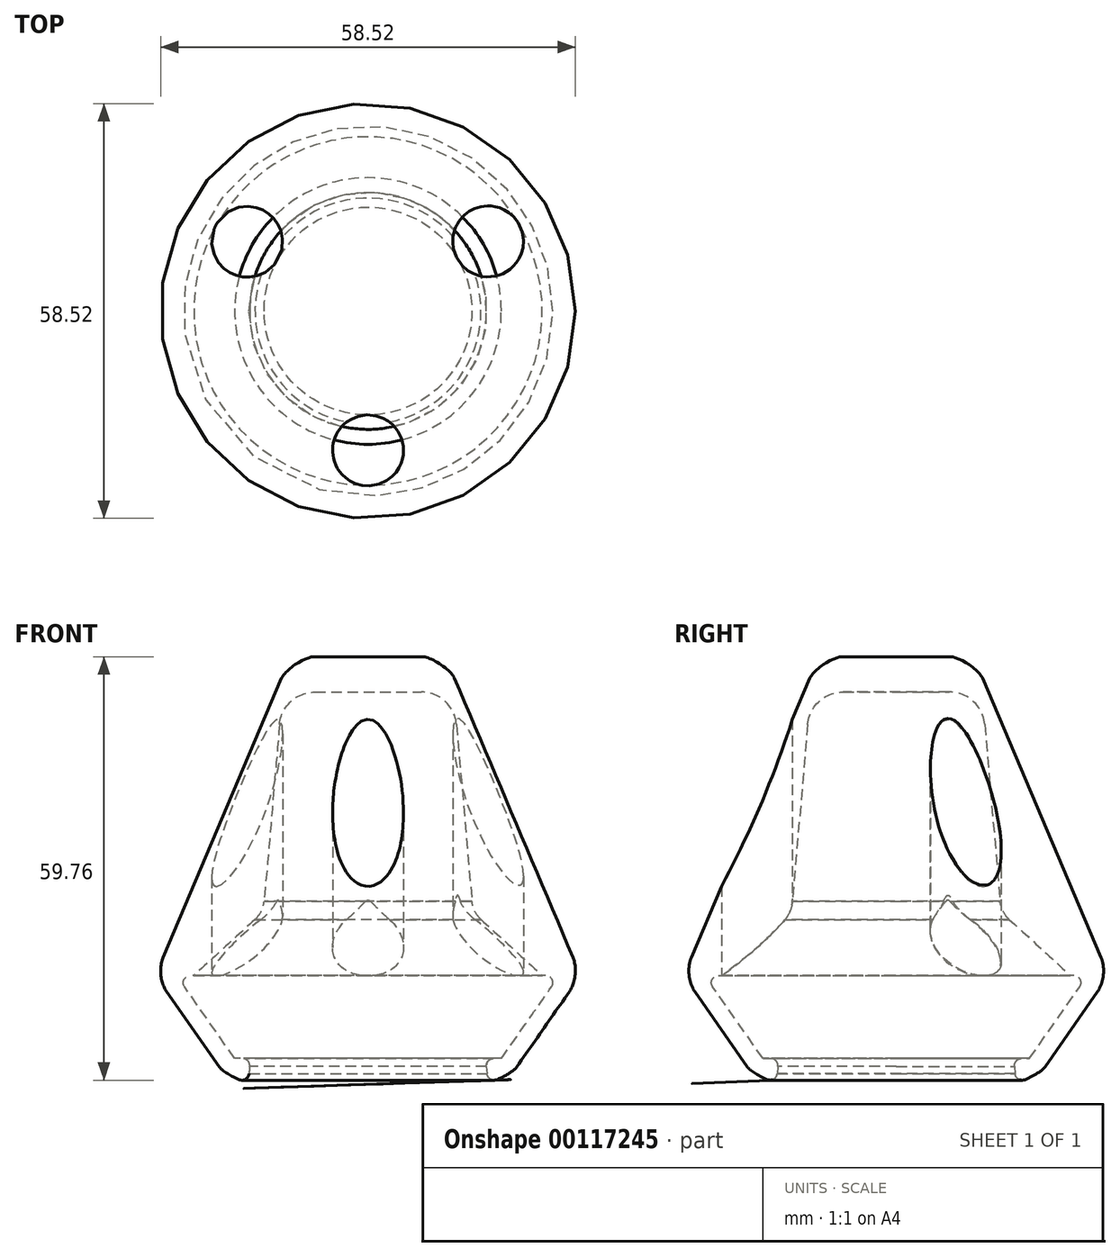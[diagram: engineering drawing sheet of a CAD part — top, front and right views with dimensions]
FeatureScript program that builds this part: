
annotation { "Feature Type Name" : "Feature", "Feature Type Description" : "" }
export const myFeature = defineFeature(function(context is Context, id is Id, definition is map)
    precondition{}
    {
        {
            var Q0;
            Q0=qCreatedBy(makeId("Top.planeOp"),FACE);
            var sketch = newSketch(context, id + "F0", { "sketchPlane" : qUnion([Q0])});
            skCircle(sketch, "E0", {"center": v(0, 0) * mm, "radius": 30 * mm});
            skCircle(sketch, "E1", {"center": v(0, -19.65) * mm, "radius": 5 * mm});
            skCircle(sketch, "E2", {"center": v(-17.05, 9.76) * mm, "radius": 5 * mm});
            skCircle(sketch, "E3", {"center": v(16.95, 9.82) * mm, "radius": 5 * mm});
            skSolve(sketch);
        }
        {
            var Q0;
            Q0=makeQuery(id+"F0.imprint","IMPRINT",FACE,{"disambiguationData":[TD([[makeQuery(id+"F0.imprint","IMPRINT",EDGE,{"derivedFrom":sQuery(id+"F0.wireOp",EDGE,"E0")}),1.0]])]});
            var Q1;
            Q1=makeQuery(id+"F0.imprint","IMPRINT",FACE,{"disambiguationData":[TD([[makeQuery(id+"F0.imprint","IMPRINT",EDGE,{"derivedFrom":sQuery(id+"F0.wireOp",EDGE,"E1")}),1.0]])]});
            var Q2;
            Q2=makeQuery(id+"F0.imprint","IMPRINT",FACE,{"disambiguationData":[TD([[makeQuery(id+"F0.imprint","IMPRINT",EDGE,{"derivedFrom":sQuery(id+"F0.wireOp",EDGE,"E3")}),1.0]])]});
            var Q3;
            Q3=makeQuery(id+"F0.imprint","IMPRINT",FACE,{"disambiguationData":[TD([[makeQuery(id+"F0.imprint","IMPRINT",EDGE,{"derivedFrom":sQuery(id+"F0.wireOp",EDGE,"E2")}),1.0]])]});
            extrude(context, id + "F1", {"entities" : qUnion([Q0, Q1, Q2, Q3]), "oppositeDirection" : true, "depth" : 15 * mm, "offsetDistance" : 25 * mm, "hasDraft" : true, "draftAngle" : 35 * degree, "draftPullDirection" : true});
        }
        {
            var Q0;
            Q0=makeQuery(id+"F0.imprint","IMPRINT",FACE,{"disambiguationData":[TD([[makeQuery(id+"F0.imprint","IMPRINT",EDGE,{"derivedFrom":sQuery(id+"F0.wireOp",EDGE,"E0")}),1.0]])]});
            var Q1;
            Q1=makeQuery(id+"F1.opExtrude","CAP_FACE",FACE,{"disambiguationData":[OSD([sQuery(id+"F0.wireOp",EDGE,"E0")])],"isStart":false});
            var Q2;
            Q2=makeQuery(id+"F0.imprint","IMPRINT",FACE,{"disambiguationData":[TD([[makeQuery(id+"F0.imprint","IMPRINT",EDGE,{"derivedFrom":sQuery(id+"F0.wireOp",EDGE,"E3")}),1.0]])]});
            var Q3;
            Q3=makeQuery(id+"F0.imprint","IMPRINT",FACE,{"disambiguationData":[TD([[makeQuery(id+"F0.imprint","IMPRINT",EDGE,{"derivedFrom":sQuery(id+"F0.wireOp",EDGE,"E1")}),1.0]])]});
            var Q4;
            Q4=makeQuery(id+"F0.imprint","IMPRINT",FACE,{"disambiguationData":[TD([[makeQuery(id+"F0.imprint","IMPRINT",EDGE,{"derivedFrom":sQuery(id+"F0.wireOp",EDGE,"E2")}),1.0]])]});
            extrude(context, id + "F2", {"entities" : qUnion([Q0, Q1, Q2, Q3, Q4]), "operationType" : NewBodyOperationType.ADD, "depth" : 45 * mm, "offsetDistance" : 25 * mm, "hasDraft" : true, "draftAngle" : 23 * degree, "draftPullDirection" : true});
        }
        {
            var Q0;
            {var subQ0=sQuery(id+"F0.wireOp",EDGE,"E0");Q0=makeQuery(id+"F2.boolean.opBoolean","MERGE",EDGE,{"derivedFrom":[makeQuery(id+"F1.opExtrude","CAP_EDGE",EDGE,{"disambiguationData":[OSD([subQ0])],"isStart":true}),makeQuery(id+"F2.opExtrude","CAP_EDGE",EDGE,{"disambiguationData":[OSD([subQ0]),TDD([makeQuery(id+"F0.imprint","IMPRINT",EDGE,{"derivedFrom":subQ0})])],"isStart":true})]});}
            fillet(context, id + "F3", {"entities" : qUnion([Q0]), "radius" : 5 * mm, "tangentPropagation" : true, "rho" : .42, "crossSection" : FilletCrossSection.CONIC, "allowEdgeOverflow" : false});
        }
        {
            var Q0;
            Q0=makeQuery(id+"F1.opExtrude","CAP_EDGE",EDGE,{"disambiguationData":[OSD([sQuery(id+"F0.wireOp",EDGE,"E0")])],"isStart":false});
            var Q1;
            {var subQ0=sQuery(id+"F0.wireOp",EDGE,"E0");Q1=makeQuery(id+"F2.opExtrude","CAP_EDGE",EDGE,{"disambiguationData":[OSD([subQ0]),TDD([makeQuery(id+"F0.imprint","IMPRINT",EDGE,{"derivedFrom":subQ0})])],"isStart":false});}
            fillet(context, id + "F4", {"entities" : qUnion([Q0, Q1]), "radius" : 5 * mm, "tangentPropagation" : true, "rho" : .3, "crossSection" : FilletCrossSection.CONIC, "allowEdgeOverflow" : false});
        }
        {
            var Q0;
            Q0=makeQuery(id+"F0.imprint","IMPRINT",FACE,{"disambiguationData":[TD([[makeQuery(id+"F0.imprint","IMPRINT",EDGE,{"derivedFrom":sQuery(id+"F0.wireOp",EDGE,"E1")}),1.0]])]});
            var Q1;
            Q1=makeQuery(id+"F0.imprint","IMPRINT",FACE,{"disambiguationData":[TD([[makeQuery(id+"F0.imprint","IMPRINT",EDGE,{"derivedFrom":sQuery(id+"F0.wireOp",EDGE,"E2")}),1.0]])]});
            var Q2;
            Q2=makeQuery(id+"F0.imprint","IMPRINT",FACE,{"disambiguationData":[TD([[makeQuery(id+"F0.imprint","IMPRINT",EDGE,{"derivedFrom":sQuery(id+"F0.wireOp",EDGE,"E3")}),1.0]])]});
            extrude(context, id + "F5", {"entities" : qUnion([Q0, Q1, Q2]), "operationType" : NewBodyOperationType.REMOVE, "endBound" : BoundingType.UP_TO_NEXT, "depth" : 25 * mm, "offsetDistance" : 25 * mm});
        }
        {
            var Q0;
            Q0=makeQuery(id+"F1.opExtrude","CAP_FACE",FACE,{"disambiguationData":[OSD([sQuery(id+"F0.wireOp",EDGE,"E0")])],"isStart":false});
            extrude(context, id + "F6", {"entities" : qUnion([Q0]), "operationType" : NewBodyOperationType.REMOVE, "oppositeDirection" : true, "depth" : 55 * mm, "offsetDistance" : 25 * mm, "hasDraft" : true, "draftAngle" : 5 * degree, "draftPullDirection" : true});
        }
        {
            var Q0;
            Q0=makeQuery(id+"F6.boolean.opBoolean","INTERSECT",EDGE,{"derivedFrom":[makeQuery(id+"F5.boolean.opBoolean","COPY",FACE,{"derivedFrom":makeQuery(id+"F5.opExtrude","CAP_FACE",FACE,{"disambiguationData":[OSD([sQuery(id+"F0.wireOp",EDGE,"E2")])],"isStart":true})}),makeQuery(id+"F6.opExtrude","SWEPT_FACE",FACE,{"disambiguationData":[OSD([sQuery(id+"F0.wireOp",EDGE,"E0")])]})]});
            var Q1;
            Q1=makeQuery(id+"F6.boolean.opBoolean","INTERSECT",EDGE,{"derivedFrom":[makeQuery(id+"F5.boolean.opBoolean","COPY",FACE,{"derivedFrom":makeQuery(id+"F5.opExtrude","CAP_FACE",FACE,{"disambiguationData":[OSD([sQuery(id+"F0.wireOp",EDGE,"E1")])],"isStart":true})}),makeQuery(id+"F6.opExtrude","SWEPT_FACE",FACE,{"disambiguationData":[OSD([sQuery(id+"F0.wireOp",EDGE,"E0")])]})]});
            var Q2;
            Q2=makeQuery(id+"F6.boolean.opBoolean","INTERSECT",EDGE,{"derivedFrom":[makeQuery(id+"F5.boolean.opBoolean","COPY",FACE,{"derivedFrom":makeQuery(id+"F5.opExtrude","CAP_FACE",FACE,{"disambiguationData":[OSD([sQuery(id+"F0.wireOp",EDGE,"E3")])],"isStart":true})}),makeQuery(id+"F6.opExtrude","SWEPT_FACE",FACE,{"disambiguationData":[OSD([sQuery(id+"F0.wireOp",EDGE,"E0")])]})]});
            chamfer(context, id + "F7", {"entities" : qUnion([Q0, Q1, Q2]), "width" : 7 * mm, "tangentPropagation" : true});
        }
        {
            var Q0;
            Q0=makeQuery(id+"F0.imprint","IMPRINT",FACE,{"disambiguationData":[TD([[makeQuery(id+"F0.imprint","IMPRINT",EDGE,{"derivedFrom":sQuery(id+"F0.wireOp",EDGE,"E0")}),1.0]])]});
            var Q1;
            Q1=makeQuery(id+"F0.imprint","IMPRINT",FACE,{"disambiguationData":[TD([[makeQuery(id+"F0.imprint","IMPRINT",EDGE,{"derivedFrom":sQuery(id+"F0.wireOp",EDGE,"E3")}),1.0]])]});
            var Q2;
            Q2=makeQuery(id+"F0.imprint","IMPRINT",FACE,{"disambiguationData":[TD([[makeQuery(id+"F0.imprint","IMPRINT",EDGE,{"derivedFrom":sQuery(id+"F0.wireOp",EDGE,"E1")}),1.0]])]});
            var Q3;
            Q3=makeQuery(id+"F0.imprint","IMPRINT",FACE,{"disambiguationData":[TD([[makeQuery(id+"F0.imprint","IMPRINT",EDGE,{"derivedFrom":sQuery(id+"F0.wireOp",EDGE,"E2")}),1.0]])]});
            extrude(context, id + "F8", {"entities" : qUnion([Q0, Q1, Q2, Q3]), "oppositeDirection" : true, "depth" : 13 * mm, "offsetDistance" : 25 * mm, "hasDraft" : true, "draftAngle" : 35 * degree, "draftPullDirection" : true});
        }
        {
            var Q0;
            Q0=makeQuery(id+"F8.opExtrude","SWEPT_BODY",BODY,{"disambiguationData":[OSD([sQuery(id+"F0.wireOp",EDGE,"E0")])]});
            var Q1;
            Q1=qCreatedBy(makeId("Origin.pointOp"),VERTEX);
            transform(context, id + "F9", {"entities" : qUnion([Q0]), "transformType" : TransformType.SCALE_UNIFORMLY, "scale" : .90, "scalePoint" : qUnion([Q1]), "makeCopy" : false});
        }
        {
            var Q0;
            Q0=makeQuery(id+"F8.opExtrude","SWEPT_BODY",BODY,{"disambiguationData":[OSD([sQuery(id+"F0.wireOp",EDGE,"E0")])]});
            var Q1;
            Q1=makeQuery(id+"F1.opExtrude","SWEPT_BODY",BODY,{"disambiguationData":[OSD([sQuery(id+"F0.wireOp",EDGE,"E0")])]});
            booleanBodies(context, id + "F10", {"operationType" : BooleanOperationType.SUBTRACTION, "tools" : qUnion([Q0]), "targets" : qUnion([Q1])});
        }
        {
            var Q0;
            {var subQ0=sQuery(id+"F0.wireOp",EDGE,"E0");Q0=makeQuery(id+"F10.opBoolean","INTERSECT",EDGE,{"disambiguationData":[OD(0.0)],"derivedFrom":[makeQuery(id+"F6.boolean.opBoolean","COPY",FACE,{"derivedFrom":makeQuery(id+"F6.opExtrude","SWEPT_FACE",FACE,{"disambiguationData":[OSD([subQ0])]})}),makeQuery(id+"F8.opExtrude","CAP_FACE",FACE,{"disambiguationData":[OSD([subQ0])],"isStart":true})]});}
            var Q1;
            {var subQ0=sQuery(id+"F0.wireOp",EDGE,"E0");Q1=makeQuery(id+"F10.opBoolean","INTERSECT",EDGE,{"disambiguationData":[OD(1.0)],"derivedFrom":[makeQuery(id+"F6.boolean.opBoolean","COPY",FACE,{"derivedFrom":makeQuery(id+"F6.opExtrude","SWEPT_FACE",FACE,{"disambiguationData":[OSD([subQ0])]})}),makeQuery(id+"F8.opExtrude","CAP_FACE",FACE,{"disambiguationData":[OSD([subQ0])],"isStart":true})]});}
            var Q2;
            {var subQ0=sQuery(id+"F0.wireOp",EDGE,"E0");Q2=makeQuery(id+"F10.opBoolean","INTERSECT",EDGE,{"disambiguationData":[OD(2.0)],"derivedFrom":[makeQuery(id+"F6.boolean.opBoolean","COPY",FACE,{"derivedFrom":makeQuery(id+"F6.opExtrude","SWEPT_FACE",FACE,{"disambiguationData":[OSD([subQ0])]})}),makeQuery(id+"F8.opExtrude","CAP_FACE",FACE,{"disambiguationData":[OSD([subQ0])],"isStart":true})]});}
            chamfer(context, id + "F11", {"entities" : qUnion([Q0, Q1, Q2]), "chamferType" : ChamferType.TWO_OFFSETS, "width1" : 9 * mm, "oppositeDirection" : false, "width2" : 9 * mm, "tangentPropagation" : true});
        }
        {
            var Q0;
            Q0=makeQuery(id+"F6.boolean.opBoolean","COPY",EDGE,{"derivedFrom":makeQuery(id+"F6.opExtrude","CAP_EDGE",EDGE,{"disambiguationData":[OSD([sQuery(id+"F0.wireOp",EDGE,"E0")])],"isStart":false})});
            fillet(context, id + "F12", {"entities" : qUnion([Q0]), "radius" : 5 * mm, "tangentPropagation" : true, "allowEdgeOverflow" : false});
        }
        {
            var Q0;
            {var subQ0=sQuery(id+"F0.wireOp",EDGE,"E0");var subQ1=makeQuery(id+"F8.opExtrude","CAP_FACE",FACE,{"disambiguationData":[OSD([subQ0])],"isStart":true});var subQ2=makeQuery(id+"F6.boolean.opBoolean","COPY",FACE,{"derivedFrom":makeQuery(id+"F6.opExtrude","SWEPT_FACE",FACE,{"disambiguationData":[OSD([subQ0])]})});Q0=makeQuery(id+"F11.opChamfer","BLEND_EDGE",EDGE,{"blendedFrom":[makeQuery(id+"F10.opBoolean","INTERSECT",EDGE,{"disambiguationData":[OD(1.0)],"derivedFrom":[subQ2,subQ1]}),makeQuery(id+"F10.opBoolean","SPLIT",FACE,{"disambiguationData":[TD([makeQuery(id+"F5.boolean.opBoolean","COPY",FACE,{"derivedFrom":makeQuery(id+"F5.opExtrude","SWEPT_FACE",FACE,{"disambiguationData":[OSD([sQuery(id+"F0.wireOp",EDGE,"E1")])]})})])],"derivedFrom":subQ2})],"blendedInto":[makeQuery(id+"F10.opBoolean","SPLIT",FACE,{"disambiguationData":[TD([makeQuery(id+"F5.boolean.opBoolean","COPY",FACE,{"derivedFrom":makeQuery(id+"F5.opExtrude","SWEPT_FACE",FACE,{"disambiguationData":[OSD([sQuery(id+"F0.wireOp",EDGE,"E1")])]})})])],"derivedFrom":subQ2})]});}
            var Q1;
            {var subQ0=sQuery(id+"F0.wireOp",EDGE,"E0");var subQ1=makeQuery(id+"F8.opExtrude","CAP_FACE",FACE,{"disambiguationData":[OSD([subQ0])],"isStart":true});var subQ2=makeQuery(id+"F6.boolean.opBoolean","COPY",FACE,{"derivedFrom":makeQuery(id+"F6.opExtrude","SWEPT_FACE",FACE,{"disambiguationData":[OSD([subQ0])]})});Q1=makeQuery(id+"F11.opChamfer","BLEND_EDGE",EDGE,{"blendedFrom":[makeQuery(id+"F10.opBoolean","INTERSECT",EDGE,{"disambiguationData":[OD(2.0)],"derivedFrom":[subQ2,subQ1]}),makeQuery(id+"F10.opBoolean","SPLIT",FACE,{"disambiguationData":[TD([makeQuery(id+"F5.boolean.opBoolean","COPY",FACE,{"derivedFrom":makeQuery(id+"F5.opExtrude","SWEPT_FACE",FACE,{"disambiguationData":[OSD([sQuery(id+"F0.wireOp",EDGE,"E1")])]})})])],"derivedFrom":subQ2})],"blendedInto":[makeQuery(id+"F10.opBoolean","SPLIT",FACE,{"disambiguationData":[TD([makeQuery(id+"F5.boolean.opBoolean","COPY",FACE,{"derivedFrom":makeQuery(id+"F5.opExtrude","SWEPT_FACE",FACE,{"disambiguationData":[OSD([sQuery(id+"F0.wireOp",EDGE,"E1")])]})})])],"derivedFrom":subQ2})]});}
            var Q2;
            {var subQ0=sQuery(id+"F0.wireOp",EDGE,"E0");var subQ1=makeQuery(id+"F8.opExtrude","CAP_FACE",FACE,{"disambiguationData":[OSD([subQ0])],"isStart":true});var subQ2=makeQuery(id+"F6.boolean.opBoolean","COPY",FACE,{"derivedFrom":makeQuery(id+"F6.opExtrude","SWEPT_FACE",FACE,{"disambiguationData":[OSD([subQ0])]})});Q2=makeQuery(id+"F11.opChamfer","BLEND_EDGE",EDGE,{"blendedFrom":[makeQuery(id+"F10.opBoolean","INTERSECT",EDGE,{"disambiguationData":[OD(0.0)],"derivedFrom":[subQ2,subQ1]}),makeQuery(id+"F10.opBoolean","SPLIT",FACE,{"disambiguationData":[TD([makeQuery(id+"F5.boolean.opBoolean","COPY",FACE,{"derivedFrom":makeQuery(id+"F5.opExtrude","SWEPT_FACE",FACE,{"disambiguationData":[OSD([sQuery(id+"F0.wireOp",EDGE,"E1")])]})})])],"derivedFrom":subQ2})],"blendedInto":[makeQuery(id+"F10.opBoolean","SPLIT",FACE,{"disambiguationData":[TD([makeQuery(id+"F5.boolean.opBoolean","COPY",FACE,{"derivedFrom":makeQuery(id+"F5.opExtrude","SWEPT_FACE",FACE,{"disambiguationData":[OSD([sQuery(id+"F0.wireOp",EDGE,"E1")])]})})])],"derivedFrom":subQ2})]});}
            fillet(context, id + "F13", {"entities" : qUnion([Q0, Q1, Q2]), "radius" : 4 * mm, "tangentPropagation" : true, "allowEdgeOverflow" : false});
        }
        {
            var Q0;
            Q0=makeQuery(id+"F10.opBoolean","COPY",EDGE,{"derivedFrom":makeQuery(id+"F8.opExtrude","CAP_EDGE",EDGE,{"disambiguationData":[OSD([sQuery(id+"F0.wireOp",EDGE,"E0")])],"isStart":true})});
            fillet(context, id + "F14", {"entities" : qUnion([Q0]), "radius" : 1 * mm, "tangentPropagation" : true, "allowEdgeOverflow" : false});
        }
        {
            var Q0;
            {var subQ0=sQuery(id+"F0.wireOp",EDGE,"E0");Q0=makeQuery(id+"F10.opBoolean","INTERSECT",EDGE,{"derivedFrom":[makeQuery(id+"F6.boolean.opBoolean","COPY",FACE,{"derivedFrom":makeQuery(id+"F6.opExtrude","SWEPT_FACE",FACE,{"disambiguationData":[OSD([subQ0])]})}),makeQuery(id+"F8.opExtrude","CAP_FACE",FACE,{"disambiguationData":[OSD([subQ0])],"isStart":false})]});}
            var Q1;
            {var subQ0=sQuery(id+"F0.wireOp",EDGE,"E0");Q1=makeQuery(id+"F6.boolean.opBoolean","MERGE",EDGE,{"derivedFrom":[makeQuery(id+"F4.opFillet","BLEND_EDGE",EDGE,{"blendedFrom":[makeQuery(id+"F1.opExtrude","CAP_EDGE",EDGE,{"disambiguationData":[OSD([subQ0])],"isStart":false}),makeQuery(id+"F1.opExtrude","CAP_FACE",FACE,{"disambiguationData":[OSD([subQ0])],"isStart":false})],"blendedInto":[makeQuery(id+"F1.opExtrude","CAP_FACE",FACE,{"disambiguationData":[OSD([subQ0])],"isStart":false})]}),makeQuery(id+"F6.opExtrude","CAP_EDGE",EDGE,{"disambiguationData":[OSD([subQ0])],"isStart":true})]});}
            fillet(context, id + "F15", {"entities" : qUnion([Q0, Q1]), "radius" : 1 * mm, "tangentPropagation" : true, "allowEdgeOverflow" : false});
        }
    });
